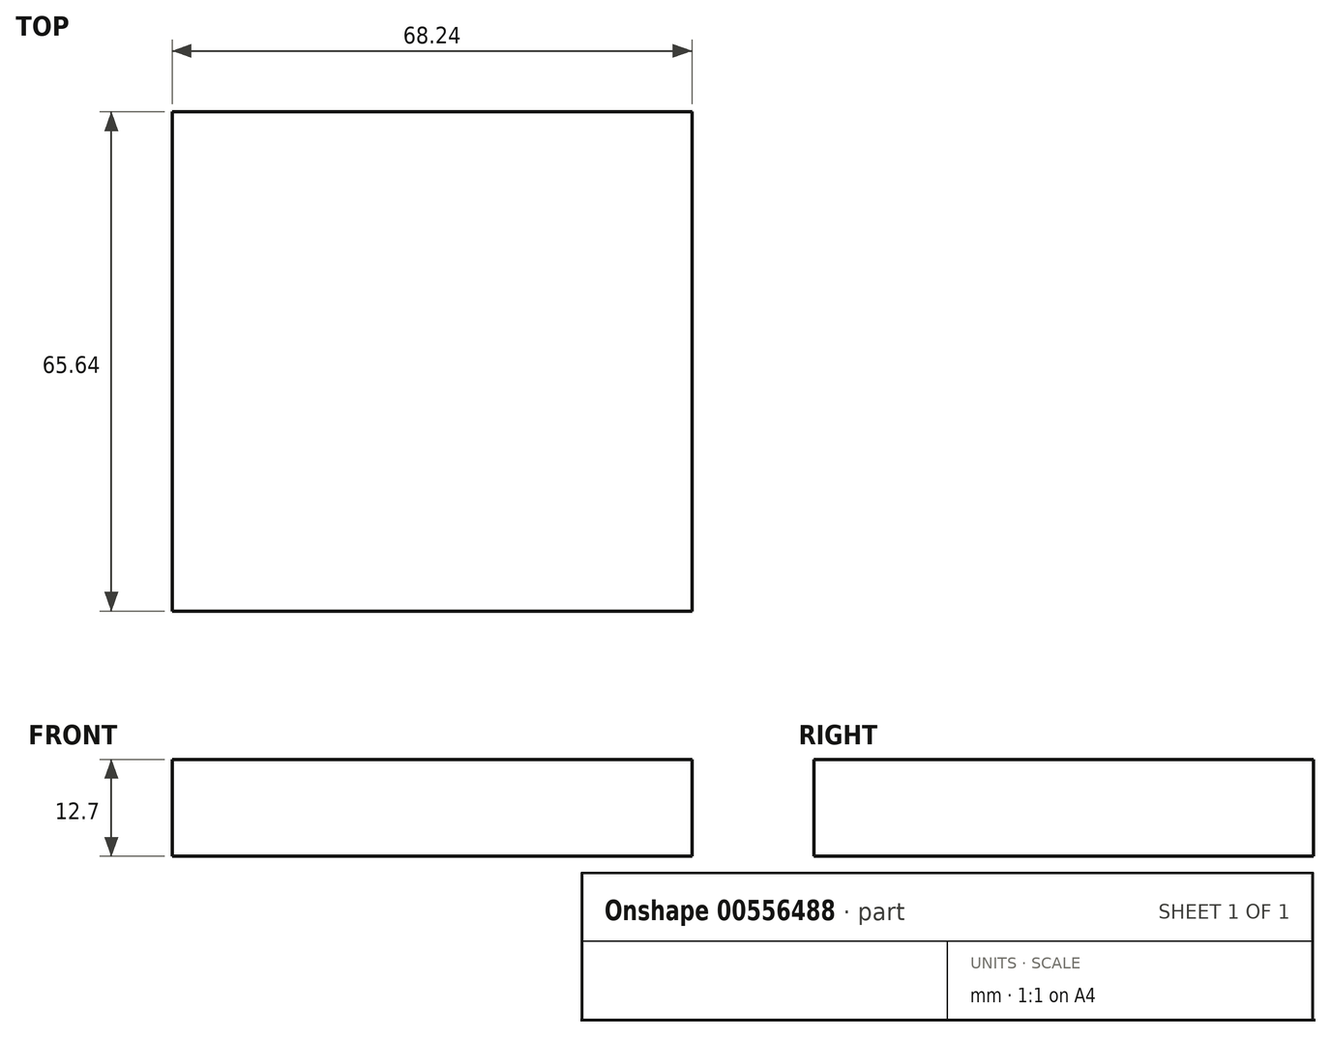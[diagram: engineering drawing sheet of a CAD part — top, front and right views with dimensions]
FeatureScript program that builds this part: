
annotation { "Feature Type Name" : "Feature", "Feature Type Description" : "" }
export const myFeature = defineFeature(function(context is Context, id is Id, definition is map)
    precondition{}
    {
        {
            var Q0;
            Q0=qCreatedBy(makeId("Top.planeOp"),FACE);
            var sketch = newSketch(context, id + "F0", { "sketchPlane" : qUnion([Q0])});
            skLineSegment(sketch, "E0.bottom", {"start": v(0, 0) * mm, "end": v(68.24, 0) * mm});
            skLineSegment(sketch, "E0.top", {"start": v(0, 65.64) * mm, "end": v(68.24, 65.64) * mm});
            skLineSegment(sketch, "E0.left", {"start": v(0, 0) * mm, "end": v(0, 65.64) * mm});
            skLineSegment(sketch, "E0.right", {"start": v(68.24, 0) * mm, "end": v(68.24, 65.64) * mm});
            skSolve(sketch);
        }
        {
            var Q0;
            Q0 = qSketchRegion(id + "F0", true);
            extrude(context, id + "F1", {"entities" : qUnion([Q0]), "depth" : 12.7 * mm, "offsetDistance" : 25.4 * mm});
        }
    });
